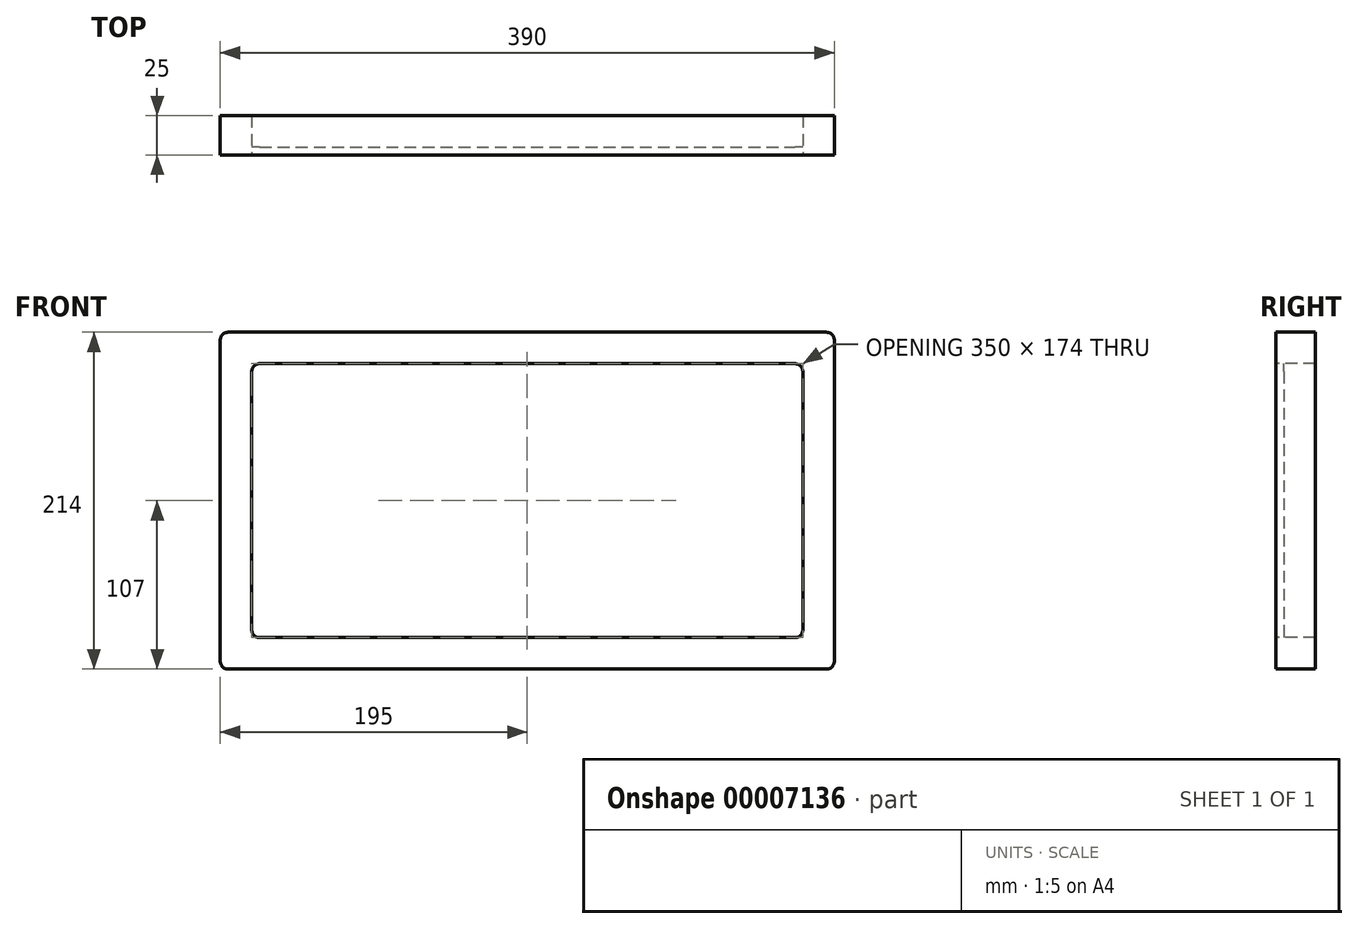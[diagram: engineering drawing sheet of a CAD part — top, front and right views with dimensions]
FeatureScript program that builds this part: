
annotation { "Feature Type Name" : "Feature", "Feature Type Description" : "" }
export const myFeature = defineFeature(function(context is Context, id is Id, definition is map)
    precondition{}
    {
        {
            var Q0;
            Q0=qCreatedBy(makeId("Front.planeOp"),FACE);
            var sketch = newSketch(context, id + "F0", { "sketchPlane" : qUnion([Q0])});
            skLineSegment(sketch, "E0.bottom", {"start": v(-190, 107) * mm, "end": v(190, 107) * mm});
            skLineSegment(sketch, "E0.top", {"start": v(-190, -107) * mm, "end": v(190, -107) * mm});
            skLineSegment(sketch, "E0.left", {"start": v(-195, 102) * mm, "end": v(-195, -102) * mm});
            skLineSegment(sketch, "E0.right", {"start": v(195, 102) * mm, "end": v(195, -102) * mm});
            skLineSegment(sketch, "E1", {"start": v(175, 82) * mm, "end": v(175, -82) * mm});
            skLineSegment(sketch, "E2", {"start": v(170, -87) * mm, "end": v(-170, -87) * mm});
            skLineSegment(sketch, "E3", {"start": v(-175, -82) * mm, "end": v(-175, 82) * mm});
            skLineSegment(sketch, "E4", {"start": v(-170, 87) * mm, "end": v(170, 87) * mm});
            skPoint(sketch, "E5.visualSharp", {"position": v(-195, 107) * mm});
            skArc(sketch, "E5.filletArc", {"start": v(-190, 107) * mm, "mid": v(-193.54, 105.54) * mm, "end": v(-195, 102) * mm});
            skPoint(sketch, "E6.visualSharp", {"position": v(-195, -107) * mm});
            skArc(sketch, "E6.filletArc", {"start": v(-195, -102) * mm, "mid": v(-193.54, -105.54) * mm, "end": v(-190, -107) * mm});
            skPoint(sketch, "E7.visualSharp", {"position": v(195, -107) * mm});
            skArc(sketch, "E7.filletArc", {"start": v(190, -107) * mm, "mid": v(193.54, -105.54) * mm, "end": v(195, -102) * mm});
            skPoint(sketch, "E8.visualSharp", {"position": v(195, 107) * mm});
            skArc(sketch, "E8.filletArc", {"start": v(195, 102) * mm, "mid": v(193.54, 105.54) * mm, "end": v(190, 107) * mm});
            skPoint(sketch, "E9.visualSharp", {"position": v(175, 87) * mm});
            skArc(sketch, "E9.filletArc", {"start": v(175, 82) * mm, "mid": v(173.54, 85.54) * mm, "end": v(170, 87) * mm});
            skPoint(sketch, "E10.visualSharp", {"position": v(175, -87) * mm});
            skArc(sketch, "E10.filletArc", {"start": v(170, -87) * mm, "mid": v(173.54, -85.54) * mm, "end": v(175, -82) * mm});
            skPoint(sketch, "E11.visualSharp", {"position": v(-175, 87) * mm});
            skArc(sketch, "E11.filletArc", {"start": v(-170, 87) * mm, "mid": v(-173.54, 85.54) * mm, "end": v(-175, 82) * mm});
            skPoint(sketch, "E12.visualSharp", {"position": v(-175, -87) * mm});
            skArc(sketch, "E12.filletArc", {"start": v(-175, -82) * mm, "mid": v(-173.54, -85.54) * mm, "end": v(-170, -87) * mm});
            skSolve(sketch);
        }
        {
            var Q0;
            Q0=makeQuery(id+"F0.imprint","IMPRINT",FACE,{"disambiguationData":[TD([[makeQuery(id+"F0.imprint","IMPRINT",EDGE,{"derivedFrom":sQuery(id+"F0.wireOp",EDGE,"E1")}),-1.0]])]});
            extrude(context, id + "F1", {"entities" : qUnion([Q0]), "oppositeDirection" : true, "depth" : 25 * mm});
        }
        {
            var Q0;
            Q0=makeQuery(id+"F1.opExtrude","CAP_FACE",FACE,{"disambiguationData":[OSD([sQuery(id+"F0.wireOp",EDGE,"E1"),sQuery(id+"F0.wireOp",EDGE,"E2"),sQuery(id+"F0.wireOp",EDGE,"E3"),sQuery(id+"F0.wireOp",EDGE,"E4")])],"isStart":true});
            extrude(context, id + "F2", {"entities" : qUnion([Q0]), "operationType" : NewBodyOperationType.REMOVE, "oppositeDirection" : true, "depth" : 5 * mm});
        }
        {
            var Q0;
            Q0 = qSketchRegion(id + "F0", true);
            extrude(context, id + "F3", {"entities" : qUnion([Q0]), "oppositeDirection" : true, "depth" : 25 * mm});
        }
    });
